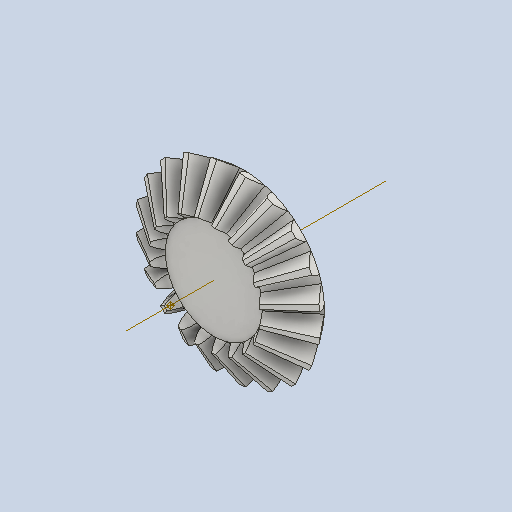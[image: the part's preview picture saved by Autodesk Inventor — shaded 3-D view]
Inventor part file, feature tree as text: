
AUTODESK INVENTOR PART (.ipt)
format: ipt  version: 2025.2 (Build 292293000, 293)  size: 470,016 bytes
history: native  units: mm
features: other x24, loft x2, pattern_circular x2
ambient origin geometry x6: Origin, XZ Plane, X Axis, Y Axis, Z Axis, Center Point
bodies: Solid1 (feature_tree)
feature tree (28):
  other  "Top Point"
  other  "Mesh Plane2"
  other  "Teeth Body"
  other  "Start Point"
  other  "Tooth Plane"
  other  "Start Sketch"
  other  "End Point"
  other  "3D Sketch Right"
  other  "End Plane Right"
  loft  "Loft Right"
  pattern_circular  "Circular Pattern Right"  [2 undecoded]
  other  "3D Sketch Left"
  other  "End Plane Left"
  loft  "Loft Left"
  pattern_circular  "Circular Pattern Left"  [2 undecoded]
  other  "Fix Body"
  other  "Mesh Plane"
  other  "Top Plane"
  other  "Teeth Body Sketch"
  other  "End Plane"
  other  "End Sketch"
  other  "Helical Curve Left"
  other  "End Sketch Left"
  other  "Body Sketch"
  other  "Srf1"
  other  "Helical Curve Right"
  other  "End Sketch Right"
  other  "Pitch Diameter"
note: 4 required parameter values undecoded (feature->parameter linkage not recoverable at this tier; creation-order binding heuristic only, values carry confidence <= 0.55)
